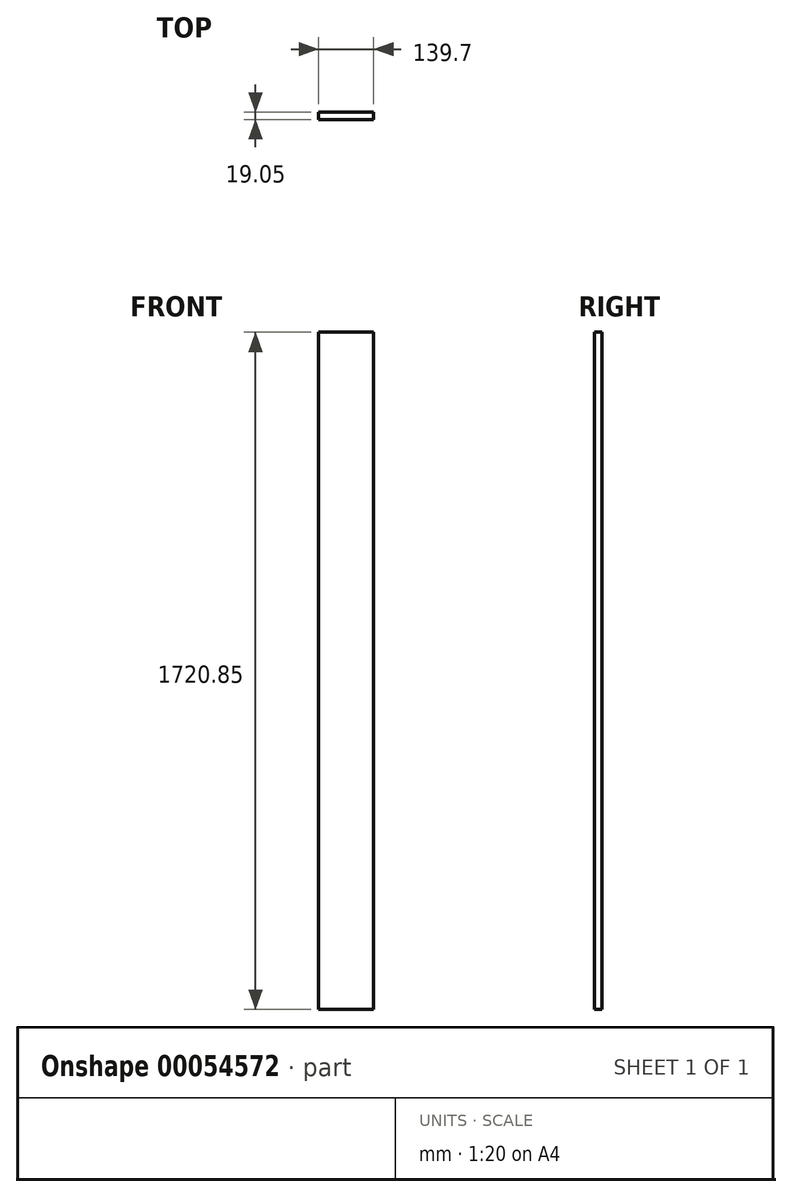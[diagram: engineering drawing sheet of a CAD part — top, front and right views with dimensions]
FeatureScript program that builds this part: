
annotation { "Feature Type Name" : "Feature", "Feature Type Description" : "" }
export const myFeature = defineFeature(function(context is Context, id is Id, definition is map)
    precondition{}
    {
        {
            var Q0;
            Q0=qCreatedBy(makeId("Top.planeOp"),FACE);
            var sketch = newSketch(context, id + "F0", { "sketchPlane" : qUnion([Q0])});
            skLineSegment(sketch, "E0.bottom", {"start": v(0, 0) * mm, "end": v(139.7, 0) * mm});
            skLineSegment(sketch, "E0.top", {"start": v(0, 19.05) * mm, "end": v(139.7, 19.05) * mm});
            skLineSegment(sketch, "E0.left", {"start": v(0, 0) * mm, "end": v(0, 19.05) * mm});
            skLineSegment(sketch, "E0.right", {"start": v(139.7, 0) * mm, "end": v(139.7, 19.05) * mm});
            skSolve(sketch);
        }
        {
            var Q0;
            Q0=makeQuery(id+"F0.imprint","IMPRINT",FACE,{"disambiguationData":[TD([[makeQuery(id+"F0.imprint","IMPRINT",EDGE,{"derivedFrom":sQuery(id+"F0.wireOp",EDGE,"E0.bottom")}),1.0]])]});
            extrude(context, id + "F1", {"entities" : qUnion([Q0]), "depth" : 1720.85 * mm});
        }
    });
